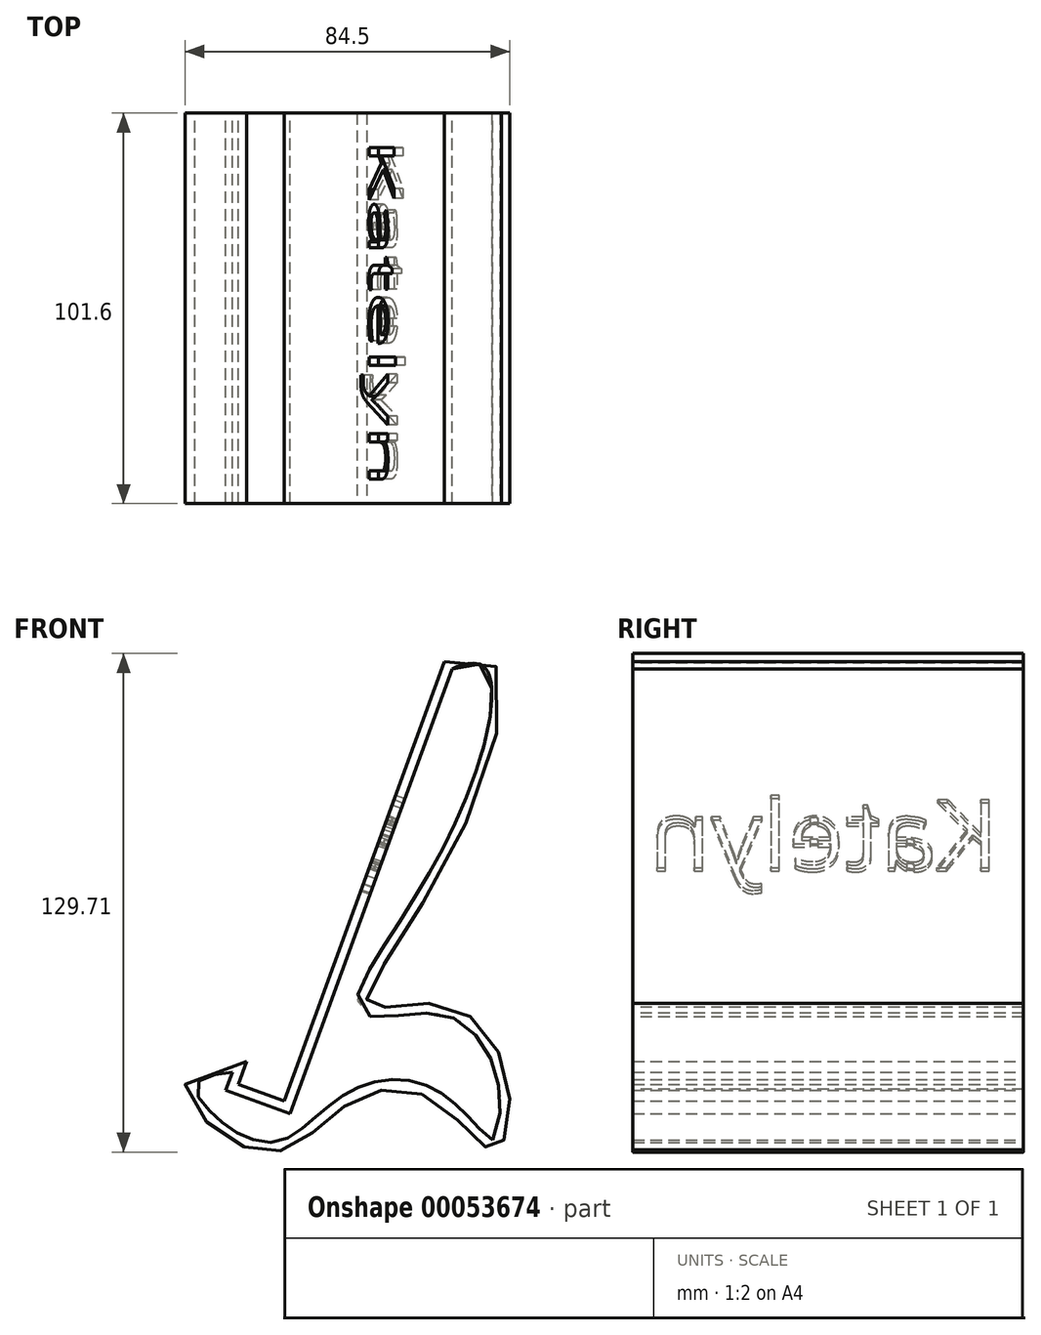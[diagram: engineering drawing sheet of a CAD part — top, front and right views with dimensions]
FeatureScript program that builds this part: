
annotation { "Feature Type Name" : "Feature", "Feature Type Description" : "" }
export const myFeature = defineFeature(function(context is Context, id is Id, definition is map)
    precondition{}
    {
        {
            var Q0;
            Q0=qCreatedBy(makeId("Front.planeOp"),FACE);
            var sketch = newSketch(context, id + "F0", { "sketchPlane" : qUnion([Q0])});
            skLineSegment(sketch, "E0.bottom", {"start": v(-76.2, 127) * mm, "end": v(0, 127) * mm, "construction": true});
            skLineSegment(sketch, "E0.top", {"start": v(-76.2, 0) * mm, "end": v(0, 0) * mm, "construction": true});
            skLineSegment(sketch, "E0.left", {"start": v(-76.2, 127) * mm, "end": v(-76.2, 0) * mm, "construction": true});
            skLineSegment(sketch, "E0.right", {"start": v(0, 127) * mm, "end": v(0, 0) * mm, "construction": true});
            skLineSegment(sketch, "E1", {"start": v(-22.66, 127) * mm, "end": v(-64.27, 12.7) * mm});
            skLineSegment(sketch, "E2", {"start": v(-64.27, 12.7) * mm, "end": v(-76.2, 17.04) * mm});
            skLineSegment(sketch, "E3", {"start": v(-76.2, 17.04) * mm, "end": v(-74.03, 23.01) * mm});
            skFitSpline(sketch, "E4", {"points": [v(-22.66, 127) * mm, v(-15.84, 87.6) * mm, v(-42.3, 37.7) * mm, v(-22.66, 37.7) * mm, v(-6, 17.04) * mm, v(-9.67, 0) * mm, v(-24.91, 12.7) * mm, v(-46.46, 12.7) * mm, v(-64.27, 0) * mm, v(-84.64, 7.46) * mm, v(-74.03, 23.01) * mm], "startDerivative": vector(503.22, 238.18) * mm, "endDerivative": vector(773.55, 27.46) * mm});
            skSolve(sketch);
        }
        {
            var Q0;
            Q0 = qSketchRegion(id + "F0", true);
            extrude(context, id + "F1", {"entities" : qUnion([Q0]), "depth" : 101.6 * mm});
        }
        {
            var Q0;
            Q0=makeQuery(id+"F1.opExtrude","CAP_FACE",FACE,{"disambiguationData":[OSD([sQuery(id+"F0.wireOp",EDGE,"E1"),sQuery(id+"F0.wireOp",EDGE,"E2"),sQuery(id+"F0.wireOp",EDGE,"E3"),sQuery(id+"F0.wireOp",EDGE,"E4")])],"isStart":false});
            var Q1;
            Q1=makeQuery(id+"F1.opExtrude","CAP_FACE",FACE,{"disambiguationData":[OSD([sQuery(id+"F0.wireOp",EDGE,"E1"),sQuery(id+"F0.wireOp",EDGE,"E2"),sQuery(id+"F0.wireOp",EDGE,"E3"),sQuery(id+"F0.wireOp",EDGE,"E4")])],"isStart":true});
            shell(context, id + "F2", {"entities" : qUnion([Q0, Q1]), "thickness" : 2.54 * mm});
        }
        {
            var Q0;
            Q0=makeQuery(id+"F1.opExtrude","SWEPT_FACE",FACE,{"disambiguationData":[OSD([sQuery(id+"F0.wireOp",EDGE,"E1")])]});
            var sketch = newSketch(context, id + "F3", { "sketchPlane" : qUnion([Q0])});
            skText(sketch, "E5", { "text": "Katelyn\n", "fontName": "OpenSans-Regular.ttf"});
            skPoint(sketch, "E6", {"position": v(50.8, 111.59) * mm});
            const initialGuessF3  = {"E5": [0.00635, 0.05452, 1, 0, 0.01897]};
            skSetInitialGuess(sketch, initialGuessF3);
            skSolve(sketch);
        }
        {
            var Q0;
            Q0 = qSketchRegion(id + "F3", true);
            extrude(context, id + "F4", {"entities" : qUnion([Q0]), "operationType" : NewBodyOperationType.REMOVE, "oppositeDirection" : true, "depth" : 2.54 * mm});
        }
        {
            var Q0;
            {var subQ2=sQuery(id+"F0.wireOp",EDGE,"E2");var subQ3=sQuery(id+"F0.wireOp",EDGE,"E1");Q0=makeQuery(id+"F4.boolean.opBoolean","SPLIT",FACE,{"disambiguationData":[TD([makeQuery(id+"F1.opExtrude","SWEPT_FACE",FACE,{"disambiguationData":[OSD([subQ2])]})])],"derivedFrom":makeQuery(id+"F1.opExtrude","SWEPT_FACE",FACE,{"disambiguationData":[OSD([subQ3])]})});}
            cPlane(context, id + "F5", {"entities" : qUnion([Q0]), "cplaneType" : CPlaneType.OFFSET, "offset" : 50.8 * mm, "oppositeDirection" : true, "width" : 152.4 * mm, "height" : 152.4 * mm});
        }
        {
            var Q0;
            {var subQ2=sQuery(id+"F0.wireOp",EDGE,"E2");var subQ3=sQuery(id+"F0.wireOp",EDGE,"E1");Q0=makeQuery(id+"F4.boolean.opBoolean","SPLIT",FACE,{"disambiguationData":[TD([makeQuery(id+"F2.opShell","OFFSET_FACE",FACE,{"disambiguationData":[OSD([subQ2])]})])],"derivedFrom":makeQuery(id+"F2.opShell","OFFSET_FACE",FACE,{"disambiguationData":[OSD([subQ3])]})});}
            var sketch = newSketch(context, id + "F6", { "sketchPlane" : qUnion([Q0])});
            skLineSegment(sketch, "E7.bottom", {"start": v(-28.5, 64.24) * mm, "end": v(-30.32, 64.24) * mm});
            skLineSegment(sketch, "E7.top", {"start": v(-28.5, 52.44) * mm, "end": v(-30.32, 52.44) * mm});
            skLineSegment(sketch, "E7.left", {"start": v(-28.5, 64.24) * mm, "end": v(-28.5, 52.44) * mm});
            skLineSegment(sketch, "E7.right", {"start": v(-30.32, 64.24) * mm, "end": v(-30.32, 52.44) * mm});
            skLineSegment(sketch, "E8.bottom", {"start": v(-53.42, 70.8) * mm, "end": v(-55.48, 70.8) * mm});
            skLineSegment(sketch, "E8.top", {"start": v(-53.42, 59.55) * mm, "end": v(-55.48, 59.55) * mm});
            skLineSegment(sketch, "E8.left", {"start": v(-53.42, 70.8) * mm, "end": v(-53.42, 59.55) * mm});
            skLineSegment(sketch, "E8.right", {"start": v(-55.48, 70.8) * mm, "end": v(-55.48, 59.55) * mm});
            skSolve(sketch);
        }
        {
            var Q0;
            Q0 = qSketchRegion(id + "F6", true);
            extrude(context, id + "F7", {"entities" : qUnion([Q0]), "operationType" : NewBodyOperationType.ADD, "oppositeDirection" : true, "depth" : 1.27 * mm});
        }
    });
